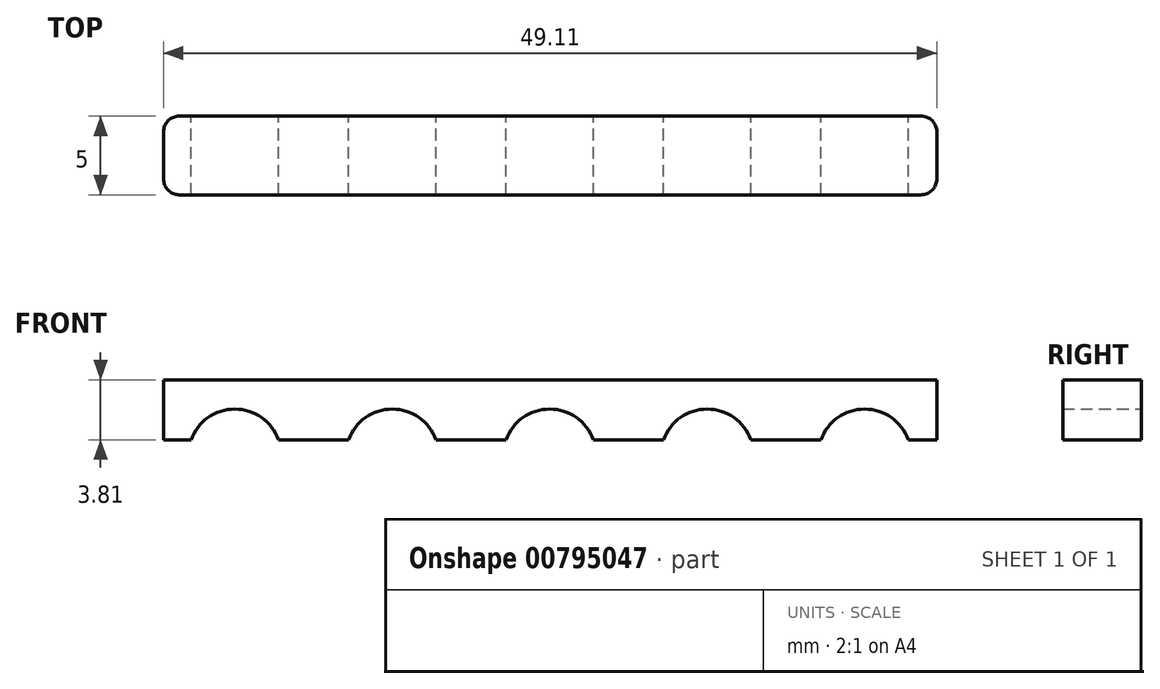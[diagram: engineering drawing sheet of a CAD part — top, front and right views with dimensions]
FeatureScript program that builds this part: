
annotation { "Feature Type Name" : "Feature", "Feature Type Description" : "" }
export const myFeature = defineFeature(function(context is Context, id is Id, definition is map)
    precondition{}
    {
        {
            var Q0;
            Q0=qCreatedBy(makeId("Front.planeOp"),FACE);
            var sketch = newSketch(context, id + "F0", { "sketchPlane" : qUnion([Q0])});
            skCircle(sketch, "E0", {"center": v(-25.6, 22.27) * mm, "radius": 2.95 * mm});
            skCircle(sketch, "E1.1.0.0", {"center": v(-15.6, 22.27) * mm, "radius": 2.95 * mm});
            skCircle(sketch, "E1.2.0.0", {"center": v(-5.6, 22.27) * mm, "radius": 2.95 * mm});
            skCircle(sketch, "E1.3.0.0", {"center": v(4.4, 22.27) * mm, "radius": 2.95 * mm});
            skCircle(sketch, "E1.4.0.0", {"center": v(14.4, 22.27) * mm, "radius": 2.95 * mm});
            skLineSegment(sketch, "E1.direction1", {"start": v(-5.31, 22.27) * mm, "end": v(4.69, 22.27) * mm, "construction": true});
            skLineSegment(sketch, "E2", {"start": v(18.98, 17.9) * mm, "end": v(-30.13, 17.9) * mm});
            skLineSegment(sketch, "E3", {"start": v(-30.13, 17.9) * mm, "end": v(-30.13, 27.08) * mm});
            skLineSegment(sketch, "E4", {"start": v(18.98, 17.9) * mm, "end": v(18.98, 27.08) * mm});
            skLineSegment(sketch, "E5", {"start": v(-30.13, 23.27) * mm, "end": v(18.98, 23.27) * mm});
            skLineSegment(sketch, "E6", {"start": v(18.98, 17.9) * mm, "end": v(18.98, 17.2) * mm});
            skLineSegment(sketch, "E7", {"start": v(18.98, 17.2) * mm, "end": v(-30.13, 17.2) * mm});
            skLineSegment(sketch, "E8", {"start": v(-30.13, 17.2) * mm, "end": v(-30.13, 17.9) * mm});
            skLineSegment(sketch, "E9", {"start": v(-30.13, 27.08) * mm, "end": v(18.98, 27.08) * mm});
            skSolve(sketch);
        }
        {
            var Q0;
            {var subQ0=sQuery(id+"F0.wireOp",EDGE,"E9");Q0=makeQuery(id+"F0.imprint","IMPRINT",FACE,{"disambiguationData":[TD([[makeQuery(id+"F0.imprint","IMPRINT",EDGE,{"derivedFrom":subQ0}),-1.0]])]});}
            extrude(context, id + "F1", {"entities" : qUnion([Q0]), "depth" : 5 * mm, "offsetDistance" : 25.4 * mm});
        }
        {
            var Q0;
            Q0=makeQuery(id+"F1.opExtrude","CAP_EDGE",EDGE,{"disambiguationData":[OSD([sQuery(id+"F0.wireOp",EDGE,"E3")])],"isStart":false});
            var Q1;
            Q1=makeQuery(id+"F1.opExtrude","CAP_EDGE",EDGE,{"disambiguationData":[OSD([sQuery(id+"F0.wireOp",EDGE,"E3")])],"isStart":true});
            var Q2;
            Q2=makeQuery(id+"F1.opExtrude","CAP_EDGE",EDGE,{"disambiguationData":[OSD([sQuery(id+"F0.wireOp",EDGE,"E4")])],"isStart":false});
            var Q3;
            Q3=makeQuery(id+"F1.opExtrude","CAP_EDGE",EDGE,{"disambiguationData":[OSD([sQuery(id+"F0.wireOp",EDGE,"E4")])],"isStart":true});
            fillet(context, id + "F2", {"entities" : qUnion([Q0, Q1, Q2, Q3]), "radius" : 1 * mm, "tangentPropagation" : true, "allowEdgeOverflow" : false});
        }
    });
